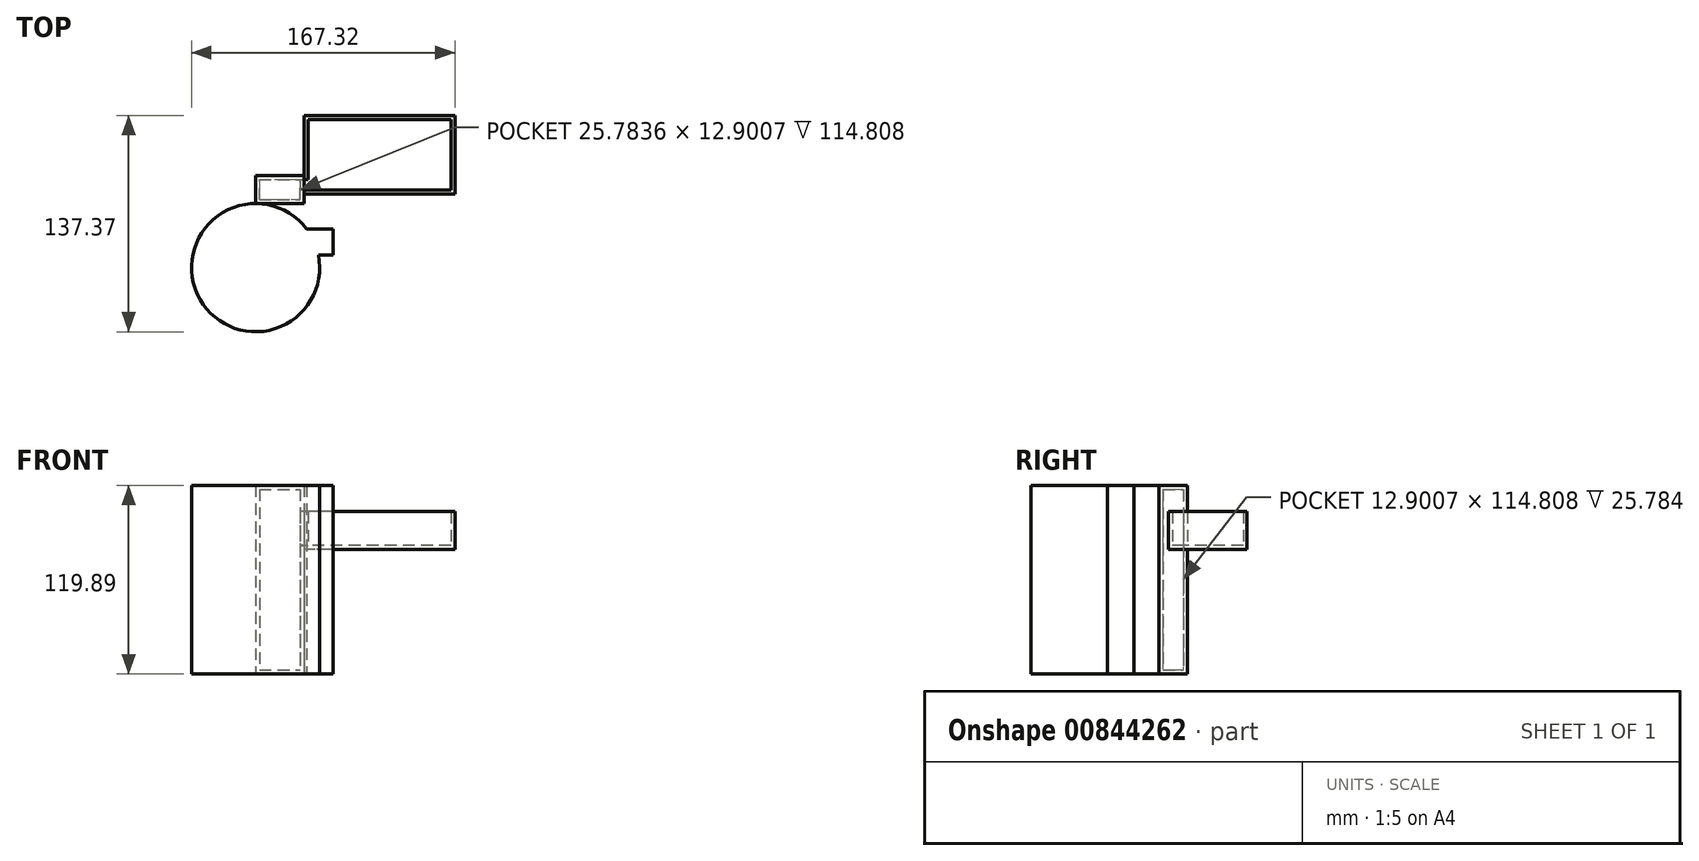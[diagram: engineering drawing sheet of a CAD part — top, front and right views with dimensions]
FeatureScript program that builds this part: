
annotation { "Feature Type Name" : "Feature", "Feature Type Description" : "" }
export const myFeature = defineFeature(function(context is Context, id is Id, definition is map)
    precondition{}
    {
        {
            var Q0;
            Q0=qCreatedBy(makeId("Top.planeOp"),FACE);
            var sketch = newSketch(context, id + "F0", { "sketchPlane" : qUnion([Q0])});
            skArc(sketch, "E0", {"start": v(32.4, 24.64) * mm, "mid": v(-37.1, -16.73) * mm, "end": v(39.92, 7.96) * mm});
            skLineSegment(sketch, "E1.bottom", {"start": v(0, 40.7) * mm, "end": v(30.86, 40.7) * mm});
            skLineSegment(sketch, "E1.top", {"start": v(0, 58.68) * mm, "end": v(30.86, 58.68) * mm});
            skLineSegment(sketch, "E1.left", {"start": v(0, 40.7) * mm, "end": v(0, 58.68) * mm});
            skLineSegment(sketch, "E1.right", {"start": v(30.86, 40.7) * mm, "end": v(30.86, 58.68) * mm});
            skLineSegment(sketch, "E2.bottom", {"start": v(49.2, 24.64) * mm, "end": v(32.4, 24.64) * mm});
            skLineSegment(sketch, "E2.top", {"start": v(49.2, 7.96) * mm, "end": v(39.92, 7.96) * mm});
            skLineSegment(sketch, "E2.left", {"start": v(49.2, 24.64) * mm, "end": v(49.2, 7.96) * mm});
            skSolve(sketch);
        }
        {
            var Q0;
            Q0 = qSketchRegion(id + "F0", true);
            extrude(context, id + "F1", {"entities" : qUnion([Q0]), "depth" : 119.89 * mm, "offsetDistance" : 25.4 * mm});
        }
        {
            var Q0;
            Q0=makeQuery(id+"F1.opExtrude","SWEPT_FACE",FACE,{"disambiguationData":[OSD([sQuery(id+"F0.wireOp",EDGE,"E1.right")])]});
            var sketch = newSketch(context, id + "F2", { "sketchPlane" : qUnion([Q0])});
            skLineSegment(sketch, "E3.bottom", {"start": v(52.98, 103.14) * mm, "end": v(46.74, 103.14) * mm});
            skLineSegment(sketch, "E3.top", {"start": v(52.98, 79) * mm, "end": v(46.74, 79) * mm});
            skLineSegment(sketch, "E3.left", {"start": v(52.98, 103.14) * mm, "end": v(52.98, 79) * mm});
            skLineSegment(sketch, "E3.right", {"start": v(46.74, 103.14) * mm, "end": v(46.74, 79) * mm});
            skSolve(sketch);
        }
        {
            var Q0;
            Q0=makeQuery(id+"F2.imprint","IMPRINT",FACE,{"disambiguationData":[TD([[makeQuery(id+"F2.imprint","IMPRINT",EDGE,{"derivedFrom":sQuery(id+"F2.wireOp",EDGE,"E3.bottom")}),1.0]])]});
            extrude(context, id + "F3", {"entities" : qUnion([Q0]), "operationType" : NewBodyOperationType.ADD, "depth" : 95.76 * mm, "offsetDistance" : 25.4 * mm});
        }
        {
            var Q0;
            Q0=makeQuery(id+"F3.opExtrude","SWEPT_FACE",FACE,{"disambiguationData":[OSD([sQuery(id+"F2.wireOp",EDGE,"E3.left")])]});
            extrude(context, id + "F4", {"entities" : qUnion([Q0]), "operationType" : NewBodyOperationType.ADD, "depth" : 43.69 * mm, "offsetDistance" : 25.4 * mm});
        }
        {
            var Q0;
            {var subQ0=sQuery(id+"F2.wireOp",EDGE,"E3.bottom");Q0=makeQuery(id+"F4.boolean.opBoolean","MERGE",FACE,{"derivedFrom":[makeQuery(id+"F3.opExtrude","SWEPT_FACE",FACE,{"disambiguationData":[OSD([subQ0])]}),makeQuery(id+"F4.opExtrude","SWEPT_FACE",FACE,{"disambiguationData":[OSD([subQ0,sQuery(id+"F2.wireOp",EDGE,"E3.left")])]})]});}
            shell(context, id + "F5", {"entities" : qUnion([Q0]), "thickness" : 2.54 * mm});
        }
    });
